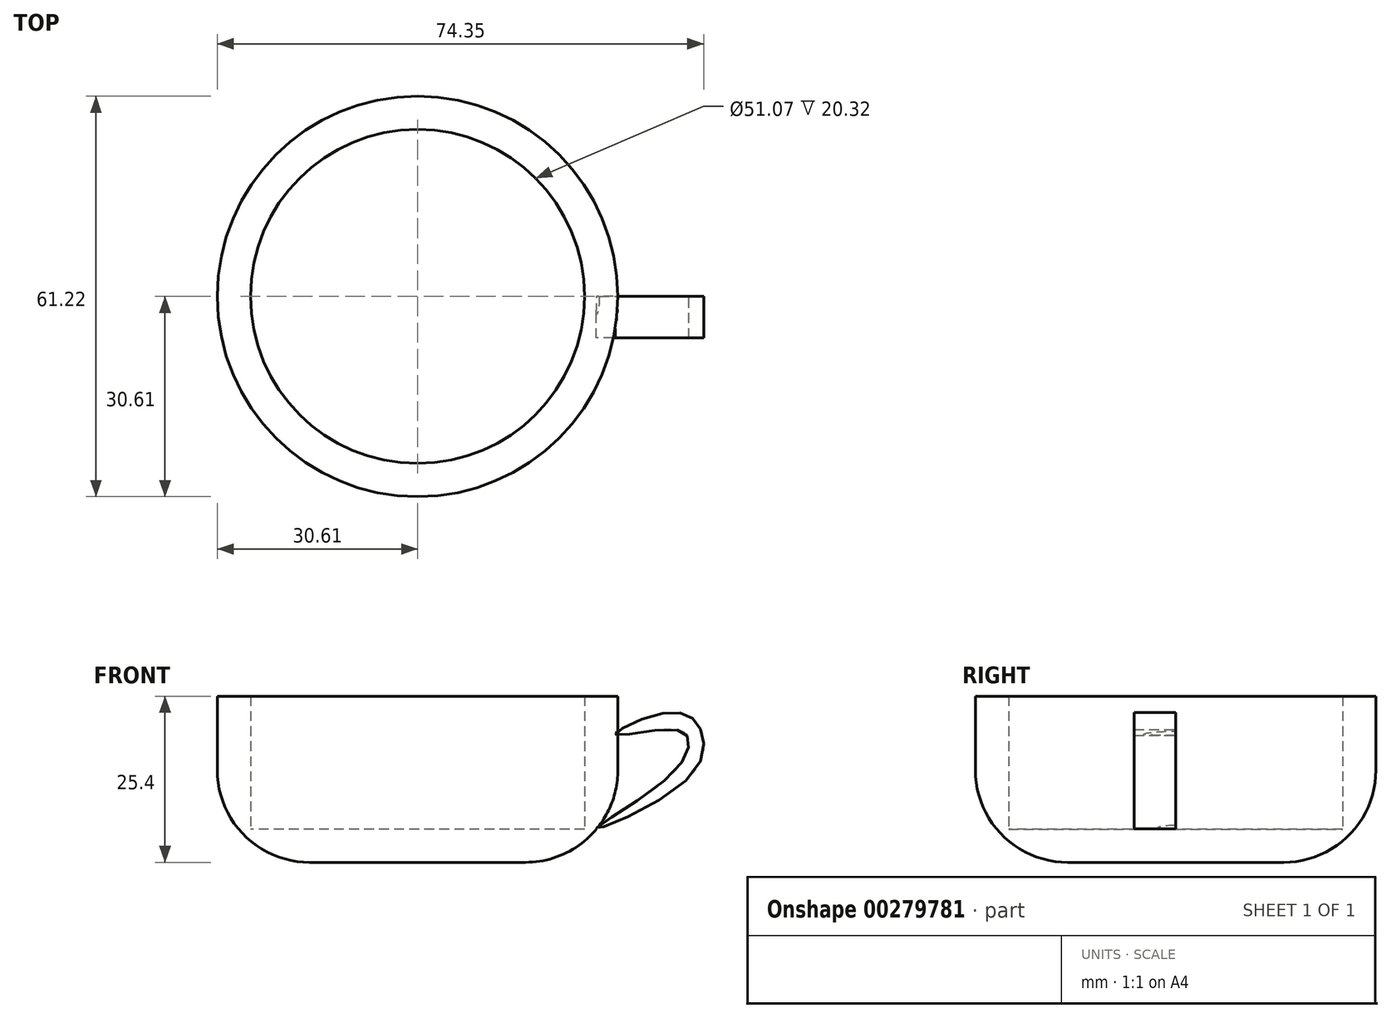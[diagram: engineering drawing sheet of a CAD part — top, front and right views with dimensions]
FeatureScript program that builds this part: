
annotation { "Feature Type Name" : "Feature", "Feature Type Description" : "" }
export const myFeature = defineFeature(function(context is Context, id is Id, definition is map)
    precondition{}
    {
        {
            var Q0;
            Q0=qCreatedBy(makeId("Top.planeOp"),FACE);
            var sketch = newSketch(context, id + "F0", { "sketchPlane" : qUnion([Q0])});
            skCircle(sketch, "E0", {"center": v(0, 0) * mm, "radius": 25.87 * mm});
            skCircle(sketch, "E1", {"center": v(0, 0) * mm, "radius": 30.61 * mm});
            skSolve(sketch);
        }
        {
            var Q0;
            Q0=makeQuery(id+"F0.imprint","IMPRINT",FACE,{"disambiguationData":[TD([[makeQuery(id+"F0.imprint","IMPRINT",EDGE,{"derivedFrom":sQuery(id+"F0.wireOp",EDGE,"E0")}),1.0]])]});
            var Q1;
            Q1=makeQuery(id+"F0.imprint","IMPRINT",FACE,{"disambiguationData":[TD([[makeQuery(id+"F0.imprint","IMPRINT",EDGE,{"derivedFrom":sQuery(id+"F0.wireOp",EDGE,"E0")}),-1.0]])]});
            extrude(context, id + "F1", {"entities" : qUnion([Q0, Q1]), "depth" : 25.4 * mm});
        }
        {
            var Q0;
            Q0=makeQuery(id+"F1.opExtrude","CAP_FACE",FACE,{"disambiguationData":[OSD([sQuery(id+"F0.wireOp",EDGE,"E1")])],"isStart":false});
            shell(context, id + "F2", {"entities" : qUnion([Q0]), "thickness" : 5.08 * mm});
        }
        {
            var Q0;
            Q0=makeQuery(id+"F1.opExtrude","CAP_EDGE",EDGE,{"disambiguationData":[OSD([sQuery(id+"F0.wireOp",EDGE,"E1")])],"isStart":true});
            fillet(context, id + "F3", {"entities" : qUnion([Q0]), "radius" : 14.1 * mm, "tangentPropagation" : true, "allowEdgeOverflow" : false});
        }
        {
            var Q0;
            Q0=qCreatedBy(makeId("Front.planeOp"),FACE);
            var sketch = newSketch(context, id + "F4", { "sketchPlane" : qUnion([Q0])});
            skFitSpline(sketch, "E2", {"points": [v(30.25, 19.5) * mm, v(35.03, 22.16) * mm, v(41.4, 22.42) * mm, v(43.52, 19.5) * mm, v(41.13, 12.6) * mm, v(27.33, 5.17) * mm, v(38.48, 13.13) * mm, v(41.4, 18.7) * mm, v(39.28, 20.3) * mm, v(30.25, 19.5) * mm]});
            skSolve(sketch);
        }
        {
            var Q0;
            Q0 = qSketchRegion(id + "F4", true);
            extrude(context, id + "F5", {"entities" : qUnion([Q0]), "operationType" : NewBodyOperationType.ADD, "depth" : 6.35 * mm});
        }
    });
